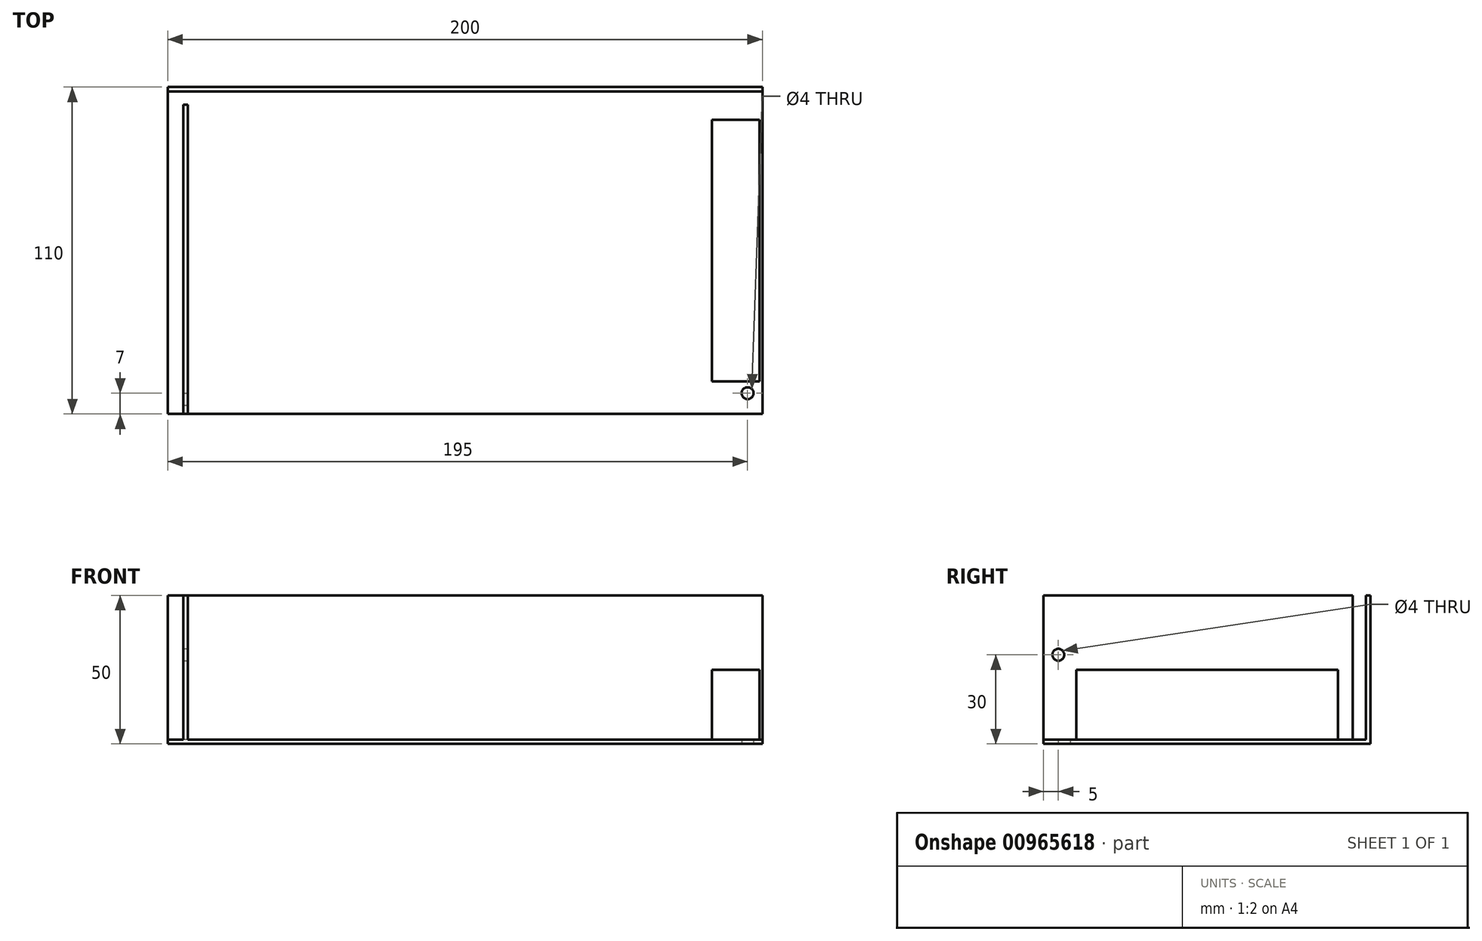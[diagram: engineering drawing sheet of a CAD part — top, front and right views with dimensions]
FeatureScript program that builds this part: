
annotation { "Feature Type Name" : "Feature", "Feature Type Description" : "" }
export const myFeature = defineFeature(function(context is Context, id is Id, definition is map)
    precondition{}
    {
        {
            var Q0;
            Q0=qCreatedBy(makeId("Top.planeOp"),FACE);
            var sketch = newSketch(context, id + "F0", { "sketchPlane" : qUnion([Q0])});
            skLineSegment(sketch, "E0.bottom", {"start": v(-100, 55) * mm, "end": v(100, 55) * mm});
            skLineSegment(sketch, "E0.top", {"start": v(-100, -55) * mm, "end": v(100, -55) * mm});
            skLineSegment(sketch, "E0.left", {"start": v(-100, 55) * mm, "end": v(-100, -55) * mm});
            skLineSegment(sketch, "E0.right", {"start": v(100, 55) * mm, "end": v(100, -55) * mm});
            skPoint(sketch, "E0.middle", {"position": v(0, 0) * mm});
            skLineSegment(sketch, "E1", {"start": v(-93.31, -55) * mm, "end": v(-93.31, 49) * mm});
            skLineSegment(sketch, "E2", {"start": v(-66, 54) * mm, "end": v(-61, 54) * mm});
            skFitSpline(sketch, "E3", {"points": [v(-61, 54) * mm, v(-58.64, 55) * mm], "startDerivative": vector(3.58, -0.02) * mm, "endDerivative": vector(3.11, 0) * mm});
            skLineSegment(sketch, "E4", {"start": v(66, 54) * mm, "end": v(71, 54) * mm});
            skFitSpline(sketch, "E5", {"points": [v(71, 54) * mm, v(72.26, 55) * mm], "startDerivative": vector(2.03, 0.08) * mm, "endDerivative": vector(1.88, 0) * mm});
            skLineSegment(sketch, "E6.bottom", {"start": v(99, 44) * mm, "end": v(83, 44) * mm});
            skLineSegment(sketch, "E6.top", {"start": v(99, -44) * mm, "end": v(83, -44) * mm});
            skLineSegment(sketch, "E6.left", {"start": v(99, 44) * mm, "end": v(99, -44) * mm});
            skLineSegment(sketch, "E6.right", {"start": v(83, 44) * mm, "end": v(83, -44) * mm});
            skCircle(sketch, "E7", {"center": v(95, -48) * mm, "radius": 2 * mm});
            skLineSegment(sketch, "E8", {"start": v(100, 53.5) * mm, "end": v(-100, 53.5) * mm});
            skLineSegment(sketch, "E9", {"start": v(-93.31, 49) * mm, "end": v(-94.81, 49) * mm});
            skLineSegment(sketch, "E10", {"start": v(-94.81, 49) * mm, "end": v(-94.81, -55) * mm});
            skSolve(sketch);
        }
        {
            var Q0;
            Q0=qCreatedBy(makeId("Right.planeOp"),FACE);
            var sketch = newSketch(context, id + "F1", { "sketchPlane" : qUnion([Q0])});
            skCircle(sketch, "E11", {"center": v(-50, 30) * mm, "radius": 2 * mm});
            skLineSegment(sketch, "E12.bottom", {"start": v(-55, 0) * mm, "end": v(55, 0) * mm});
            skLineSegment(sketch, "E12.top", {"start": v(-55, 50) * mm, "end": v(55, 50) * mm});
            skLineSegment(sketch, "E12.left", {"start": v(-55, 0) * mm, "end": v(-55, 50) * mm});
            skLineSegment(sketch, "E12.right", {"start": v(55, 0) * mm, "end": v(55, 50) * mm});
            skLineSegment(sketch, "E13", {"start": v(-55, 15) * mm, "end": v(49, 15) * mm});
            skSolve(sketch);
        }
        {
            var Q0;
            {var subQ0=sQuery(id+"F0.wireOp",EDGE,"E1");Q0=makeQuery(id+"F0.imprint","IMPRINT",FACE,{"disambiguationData":[TD([[makeQuery(id+"F0.imprint","IMPRINT",EDGE,{"derivedFrom":subQ0}),-1.0]])]});}
            var Q1;
            Q1=makeQuery(id+"F0.imprint","IMPRINT",FACE,{"disambiguationData":[TD([[makeQuery(id+"F0.imprint","IMPRINT",EDGE,{"derivedFrom":sQuery(id+"F0.wireOp",EDGE,"E6.bottom")}),1.0]])]});
            extrude(context, id + "F2", {"entities" : qUnion([Q0, Q1]), "depth" : 1.5 * mm, "offsetDistance" : 25 * mm});
        }
        {
            var Q0;
            {var subQ6=sQuery(id+"F0.wireOp",EDGE,"E8");Q0=makeQuery(id+"F0.imprint","IMPRINT",FACE,{"disambiguationData":[TD([[makeQuery(id+"F0.imprint","IMPRINT",EDGE,{"derivedFrom":subQ6}),-1.0]])]});}
            var Q1;
            {var subQ0=sQuery(id+"F0.wireOp",EDGE,"E1");Q1=makeQuery(id+"F0.imprint","IMPRINT",FACE,{"disambiguationData":[TD([[makeQuery(id+"F0.imprint","IMPRINT",EDGE,{"derivedFrom":subQ0}),1.0]])]});}
            extrude(context, id + "F3", {"entities" : qUnion([Q0, Q1]), "operationType" : NewBodyOperationType.ADD, "depth" : 50 * mm, "offsetDistance" : 25 * mm});
        }
        {
            var Q0;
            Q0=makeQuery(id+"F0.imprint","IMPRINT",FACE,{"disambiguationData":[TD([[makeQuery(id+"F0.imprint","IMPRINT",EDGE,{"derivedFrom":sQuery(id+"F0.wireOp",EDGE,"E6.bottom")}),1.0]])]});
            extrude(context, id + "F4", {"entities" : qUnion([Q0]), "operationType" : NewBodyOperationType.ADD, "depth" : 25 * mm, "offsetDistance" : 25 * mm});
        }
        {
            var Q0;
            Q0=sQuery(id+"F1.wireOp",VERTEX,"E11.center");
            var Q1;
            Q1=makeQuery(id+"F2.opExtrude","SWEPT_BODY",BODY,{"disambiguationData":[OSD([sQuery(id+"F0.wireOp",EDGE,"E0.top"),sQuery(id+"F0.wireOp",EDGE,"E0.left"),sQuery(id+"F0.wireOp",EDGE,"E0.right"),sQuery(id+"F0.wireOp",EDGE,"E1"),sQuery(id+"F0.wireOp",EDGE,"E7"),sQuery(id+"F0.wireOp",EDGE,"E8"),sQuery(id+"F0.wireOp",EDGE,"E9"),sQuery(id+"F0.wireOp",EDGE,"E10")])]});
            hole(context, id + "F5", {"style" : HoleStyle.SIMPLE, "endStyle" : HoleEndStyle.THROUGH, "holeDiameter" : 4 * mm, "majorDiameter" : 5 * mm, "isTappedThrough" : true, "tappedDepth" : 12 * mm, "tapClearance" : 3, "locations" : qUnion([Q0]), "scope" : qUnion([Q1])});
        }
        {
            var Q0;
            Q0=sQuery(id+"F0.wireOp",EDGE,"E2");
            var Q1;
            Q1=sQuery(id+"F0.wireOp",EDGE,"E3");
            var Q2;
            Q2=sQuery(id+"F0.wireOp",EDGE,"E4");
            var Q3;
            Q3=sQuery(id+"F0.wireOp",EDGE,"E5");
            extrude(context, id + "F6", {"bodyType" : ToolBodyType.SURFACE, "surfaceEntities" : qUnion([Q0, Q1, Q2, Q3]), "depth" : 47 * mm, "offsetDistance" : 25 * mm, "hasSecondDirection" : true, "secondDirectionOppositeDirection" : false, "secondDirectionDepth" : 43 * mm});
        }
    });
